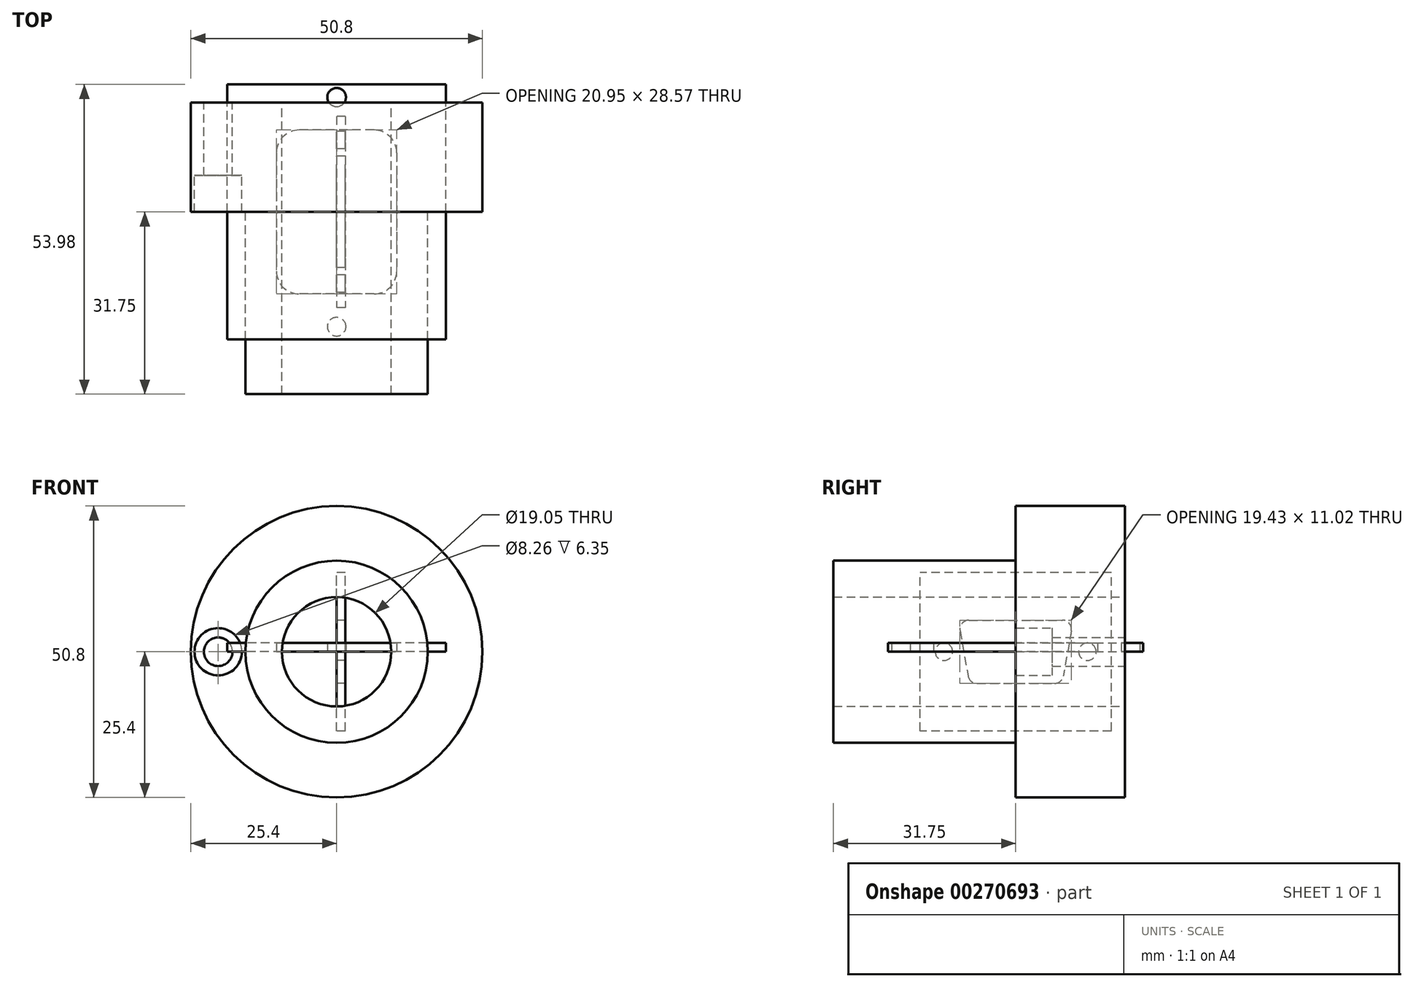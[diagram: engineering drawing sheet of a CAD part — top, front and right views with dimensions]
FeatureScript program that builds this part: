
annotation { "Feature Type Name" : "Feature", "Feature Type Description" : "" }
export const myFeature = defineFeature(function(context is Context, id is Id, definition is map)
    precondition{}
    {
        {
            var Q0;
            Q0=qCreatedBy(makeId("Front.planeOp"),FACE);
            var sketch = newSketch(context, id + "F0", { "sketchPlane" : qUnion([Q0])});
            skCircle(sketch, "E0", {"center": v(0, 0) * mm, "radius": 25.4 * mm});
            skCircle(sketch, "E1", {"center": v(0, 0) * mm, "radius": 15.88 * mm});
            skCircle(sketch, "E2", {"center": v(0, 0) * mm, "radius": 9.53 * mm});
            skLineSegment(sketch, "E3", {"start": v(-25.4, 0) * mm, "end": v(-15.88, 0) * mm});
            skPoint(sketch, "E4", {"position": v(-20.64, 0) * mm});
            skSolve(sketch);
        }
        {
            var Q0;
            Q0=makeQuery(id+"F0.imprint","IMPRINT",FACE,{"disambiguationData":[TD([[makeQuery(id+"F0.imprint","IMPRINT",EDGE,{"derivedFrom":sQuery(id+"F0.wireOp",EDGE,"E1")}),1.0]])]});
            extrude(context, id + "F1", {"entities" : qUnion([Q0]), "depth" : 31.75 * mm});
        }
        {
            var Q0;
            Q0=makeQuery(id+"F0.imprint","IMPRINT",FACE,{"disambiguationData":[TD([[makeQuery(id+"F0.imprint","IMPRINT",EDGE,{"derivedFrom":sQuery(id+"F0.wireOp",EDGE,"E0")}),1.0]])]});
            var Q1;
            Q1=makeQuery(id+"F0.imprint","IMPRINT",FACE,{"disambiguationData":[TD([[makeQuery(id+"F0.imprint","IMPRINT",EDGE,{"derivedFrom":sQuery(id+"F0.wireOp",EDGE,"E1")}),1.0]])]});
            extrude(context, id + "F2", {"entities" : qUnion([Q0, Q1]), "operationType" : NewBodyOperationType.ADD, "oppositeDirection" : true, "depth" : 19.05 * mm});
        }
        {
            var Q0;
            Q0=sQuery(id+"F0.wireOp",VERTEX,"E4");
            var Q1;
            Q1=makeQuery(id+"F1.opExtrude","SWEPT_BODY",BODY,{"disambiguationData":[OSD([sQuery(id+"F0.wireOp",EDGE,"E1"),sQuery(id+"F0.wireOp",EDGE,"E2")])]});
            hole(context, id + "F3", {"style" : HoleStyle.C_BORE, "endStyle" : HoleEndStyle.THROUGH, "holeDiameter" : 4.98 * mm, "cBoreDiameter" : 8.25 * mm, "cBoreDepth" : 6.35 * mm, "tappedDepth" : 10.3 * mm, "tapClearance" : 3, "locations" : qUnion([Q0]), "scope" : qUnion([Q1]), "startStyle" : HoleStartStyle.PART});
        }
        {
            var Q0;
            Q0=qCreatedBy(makeId("Right.planeOp"),FACE);
            var sketch = newSketch(context, id + "F4", { "sketchPlane" : qUnion([Q0])});
            skLineSegment(sketch, "E5", {"start": v(-8.13, 5.51) * mm, "end": v(8.13, 5.51) * mm});
            skLineSegment(sketch, "E6", {"start": v(-6.74, -5.51) * mm, "end": v(6.74, -5.51) * mm});
            skCircle(sketch, "E7", {"center": v(8.13, 3.92) * mm, "radius": 1.59 * mm});
            skCircle(sketch, "E8", {"center": v(-8.13, 3.92) * mm, "radius": 1.59 * mm});
            skLineSegment(sketch, "E9", {"start": v(-9.7, 3.65) * mm, "end": v(-8.3, -4.2) * mm});
            skLineSegment(sketch, "E10", {"start": v(9.7, 3.65) * mm, "end": v(8.3, -4.2) * mm});
            skCircle(sketch, "E11", {"center": v(-6.74, -3.92) * mm, "radius": 1.59 * mm});
            skCircle(sketch, "E12", {"center": v(6.74, -3.92) * mm, "radius": 1.59 * mm});
            skCircle(sketch, "E13", {"center": v(-12.5, 0) * mm, "radius": 1.52 * mm});
            skCircle(sketch, "E14", {"center": v(12.5, 0) * mm, "radius": 1.52 * mm});
            skLineSegment(sketch, "E15.bottom", {"start": v(16.68, -13.81) * mm, "end": v(-16.68, -13.81) * mm});
            skLineSegment(sketch, "E15.top", {"start": v(16.68, 13.81) * mm, "end": v(-16.68, 13.81) * mm});
            skLineSegment(sketch, "E15.left", {"start": v(16.68, -13.81) * mm, "end": v(16.68, 13.81) * mm});
            skLineSegment(sketch, "E15.right", {"start": v(-16.68, -13.81) * mm, "end": v(-16.68, 13.81) * mm});
            skPoint(sketch, "E15.middle", {"position": v(0, 0) * mm});
            skSolve(sketch);
        }
        {
            var Q0;
            {var subQ5=sQuery(id+"F4.wireOp",EDGE,"E5");Q0=makeQuery(id+"F4.imprint","IMPRINT",FACE,{"disambiguationData":[TD([[makeQuery(id+"F4.imprint","IMPRINT",EDGE,{"derivedFrom":subQ5}),1.0]])]});}
            extrude(context, id + "F5", {"entities" : qUnion([Q0]), "depth" : 1.52 * mm});
        }
        {
            var Q0;
            Q0=qCreatedBy(makeId("Top.planeOp"),FACE);
            var sketch = newSketch(context, id + "F6", { "sketchPlane" : qUnion([Q0])});
            skLineSegment(sketch, "E16.bottom", {"start": v(6.5, 14.29) * mm, "end": v(-6.5, 14.29) * mm});
            skLineSegment(sketch, "E16.top", {"start": v(6.5, -14.29) * mm, "end": v(-6.5, -14.29) * mm});
            skLineSegment(sketch, "E16.left", {"start": v(10.48, 10.32) * mm, "end": v(10.48, -10.32) * mm});
            skLineSegment(sketch, "E16.right", {"start": v(-10.48, 10.32) * mm, "end": v(-10.48, -10.32) * mm});
            skPoint(sketch, "E16.middle", {"position": v(0, 0) * mm});
            skPoint(sketch, "E17.visualSharp", {"position": v(-10.48, 14.29) * mm});
            skArc(sketch, "E17.filletArc", {"start": v(-6.5, 14.29) * mm, "mid": v(-9.32, 13.13) * mm, "end": v(-10.48, 10.32) * mm});
            skPoint(sketch, "E18.visualSharp", {"position": v(10.48, 14.29) * mm});
            skArc(sketch, "E18.filletArc", {"start": v(10.48, 10.32) * mm, "mid": v(9.32, 13.13) * mm, "end": v(6.5, 14.29) * mm});
            skPoint(sketch, "E19.visualSharp", {"position": v(10.48, -14.29) * mm});
            skArc(sketch, "E19.filletArc", {"start": v(6.5, -14.29) * mm, "mid": v(9.32, -13.13) * mm, "end": v(10.48, -10.32) * mm});
            skPoint(sketch, "E20.visualSharp", {"position": v(-10.48, -14.29) * mm});
            skArc(sketch, "E20.filletArc", {"start": v(-10.48, -10.32) * mm, "mid": v(-9.32, -13.13) * mm, "end": v(-6.5, -14.29) * mm});
            skLineSegment(sketch, "E21.bottom", {"start": v(19.05, -22.22) * mm, "end": v(-19.05, -22.23) * mm});
            skLineSegment(sketch, "E21.top", {"start": v(19.05, 22.23) * mm, "end": v(-19.05, 22.22) * mm});
            skLineSegment(sketch, "E21.left", {"start": v(19.05, -22.22) * mm, "end": v(19.05, 22.23) * mm});
            skLineSegment(sketch, "E21.right", {"start": v(-19.05, -22.23) * mm, "end": v(-19.05, 22.22) * mm});
            skCircle(sketch, "E22", {"center": v(0, 19.99) * mm, "radius": 1.63 * mm});
            skCircle(sketch, "E23", {"center": v(0, -19.99) * mm, "radius": 1.63 * mm});
            skSolve(sketch);
        }
        {
            var Q0;
            Q0=makeQuery(id+"F6.imprint","IMPRINT",FACE,{"disambiguationData":[TD([[makeQuery(id+"F6.imprint","IMPRINT",EDGE,{"derivedFrom":sQuery(id+"F6.wireOp",EDGE,"E16.bottom")}),-1.0]])]});
            extrude(context, id + "F7", {"entities" : qUnion([Q0]), "depth" : 1.57 * mm});
        }
    });
